# Revit family: LDA_BIM_MICROFONO-UNIDAD EXPANSION_MPS-8K
name_source: partatom
category: Equipos especializados
units: mm (PartAtom-declared; Revit-internal decimal feet)

## family parameters
Compartido = No
Corte con vacíos al cargar = Sí
Cota de conector redondo = Diámetro de uso
Número OmniClass = 23.85.05.17
Punto de cálculo de habitación = No
Se basa en plano de trabajo = Sí
Siempre vertical = No
Tipo de pieza = Normal
Título OmniClass = Complete Audio-Visual Systems

## types (1)
- MPS-8K
    Accesorios = Elementos de anclaje y conexión a MPS-8Z y etiqueta para identificador de botón
    Botones = 8 x selección de zona
    Color = Gris RAL 7016 y Negro RAL 9005
    Condiciones de funcionamiento = Entre -5ºC y +45ºC / 23ºF y 113ºF 5
    Descripción = Unidad de expansión modelo LDA MPS-8K para el micrófono de megafonía MPS-8Z.
    Dimensiones (W x H x D) = 86 x 75 x 200 mm / 3.4" x 2.9" x 7.9"
    Dimensiones embalaje (W x H x D) = 380 x 100 x 320 mm / 15" x 3.9" x 12.6"
    Elevación por defecto = 0 mm  [stored 0 ft]
    Fabricante = LDA
    Imagen de tipo = <Ninguno>
    Material = Fe 1,5 mm / 0,15"
    Modelo = MPS-8K
    Peso bruto = 1,2 Kg / 2.6 lb
    Peso neto = 0,85 Kg / 1.9 lb
    Referencia = LDAMPS8KS01
    URL = http://support.lda-audiotech.com

note: [stored X ft] marks values corroborated as IEEE doubles in the binary element streams (Revit-internal decimal feet)
